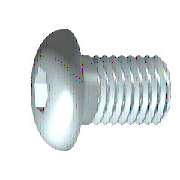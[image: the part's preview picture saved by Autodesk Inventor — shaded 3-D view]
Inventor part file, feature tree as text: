
AUTODESK INVENTOR PART (.ipt)
format: ipt  version: 2017.1 (Build 211199000, 199)  size: 198,656 bytes
history: native  units: mm (DEFAULTED — no unit token found)
features: sketch x2, extrude x1, plane x1, fillet x1
ambient origin geometry x7: Origin, YZ Plane, XY Plane, X Axis, Y Axis, Z Axis, Center Point
bodies: Solid1 (feature_tree), Body (feature_tree)
feature tree (5):
  extrude  "Slot"  Depth=1.8542mm
  plane  "Work Plane1"
  fillet  "Fillet2"  Radius=1.8542mm
  sketch  "Sketch1"  dims[d1=4.75976mm d2=1.59014mm d3=1.8542mm]
  sketch  "Sketch2"  dims[d4=1.1176mm d5=60.0deg d6=3.5052mm d7=3.5052mm d8=2.287693mm d9=6.6548mm d10=90.0deg d11=10.0mm d12=0.0mm d13=4.75976mm d14=0.0mm d15=0.486918mm d16=0.486918mm d17=1.6002mm d19=0.0mm d26=6.35mm d27=45.0deg d28=0.0mm d29=0.0mm d30=0.1mm]
